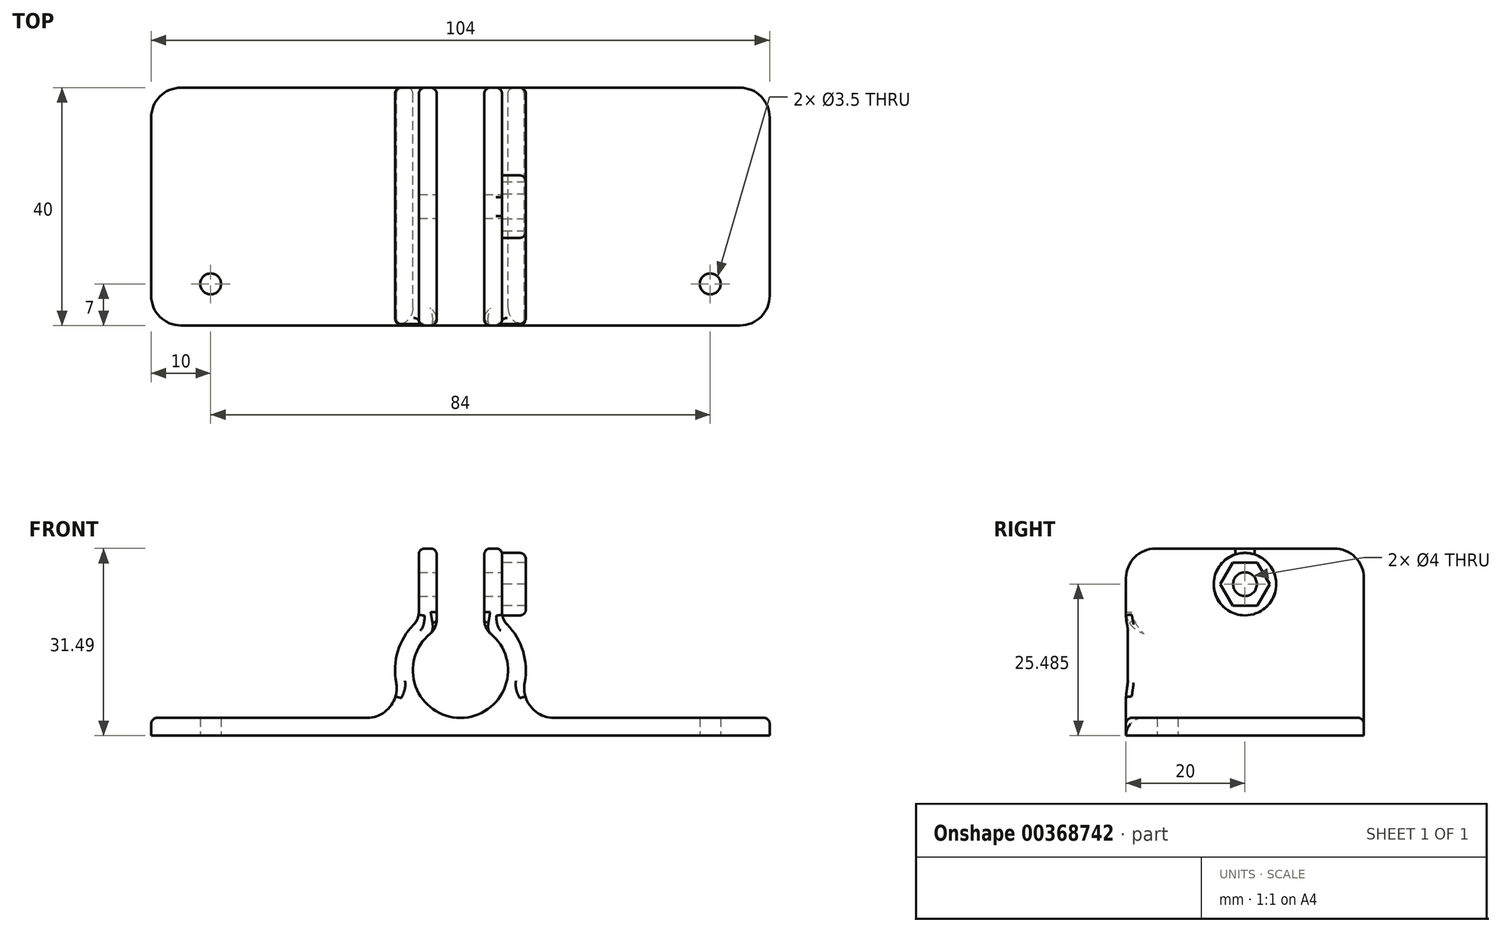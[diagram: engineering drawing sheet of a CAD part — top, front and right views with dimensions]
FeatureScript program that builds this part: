
annotation { "Feature Type Name" : "Feature", "Feature Type Description" : "" }
export const myFeature = defineFeature(function(context is Context, id is Id, definition is map)
    precondition{}
    {
        {
            var Q0;
            Q0=qCreatedBy(makeId("Top.planeOp"),FACE);
            var sketch = newSketch(context, id + "F0", { "sketchPlane" : qUnion([Q0])});
            skLineSegment(sketch, "E0.bottom", {"start": v(-52, 20) * mm, "end": v(52, 20) * mm});
            skLineSegment(sketch, "E0.top", {"start": v(-52, -20) * mm, "end": v(52, -20) * mm});
            skLineSegment(sketch, "E0.left", {"start": v(-52, 20) * mm, "end": v(-52, -20) * mm});
            skLineSegment(sketch, "E0.right", {"start": v(52, 20) * mm, "end": v(52, -20) * mm});
            skPoint(sketch, "E0.middle", {"position": v(0, 0) * mm});
            skLineSegment(sketch, "E1", {"start": v(-63.76, -13) * mm, "end": v(70.54, -13) * mm, "construction": true});
            skCircle(sketch, "E2", {"center": v(-42, -13) * mm, "radius": 1.75 * mm});
            skCircle(sketch, "E3.MirrorC", {"center": v(42, -13) * mm, "radius": 1.75 * mm});
            skSolve(sketch);
        }
        {
            var Q0;
            Q0=qCreatedBy(makeId("Front.planeOp"),FACE);
            cPlane(context, id + "F1", {"entities" : qUnion([Q0]), "cplaneType" : CPlaneType.OFFSET, "offset" : 20 * mm, "oppositeDirection" : true, "width" : 150 * mm, "height" : 150 * mm});
        }
        {
            var Q0;
            Q0=qCreatedBy(id+"F1.planeOp",FACE);
            var sketch = newSketch(context, id + "F2", { "sketchPlane" : qUnion([Q0])});
            skCircle(sketch, "E4", {"center": v(0, 11) * mm, "radius": 11 * mm});
            skPoint(sketch, "E4.first.point", {"position": v(0, 0) * mm});
            skPoint(sketch, "E4.second.point", {"position": v(0, 22) * mm});
            skCircle(sketch, "E5", {"center": v(0, 11) * mm, "radius": 8 * mm});
            skLineSegment(sketch, "E6.bottom", {"start": v(-7, 14.87) * mm, "end": v(-4, 14.87) * mm});
            skLineSegment(sketch, "E6.top", {"start": v(-7, 31.49) * mm, "end": v(-4, 31.49) * mm});
            skLineSegment(sketch, "E6.left", {"start": v(-7, 14.87) * mm, "end": v(-7, 31.49) * mm});
            skLineSegment(sketch, "E6.right", {"start": v(-4, 14.87) * mm, "end": v(-4, 31.49) * mm});
            skPoint(sketch, "E7", {"position": v(-7, 19.49) * mm});
            skLineSegment(sketch, "E8.MirrorCS", {"start": v(4, 14.87) * mm, "end": v(4, 31.49) * mm});
            skLineSegment(sketch, "E9.MirrorCS", {"start": v(7, 31.49) * mm, "end": v(4, 31.49) * mm});
            skLineSegment(sketch, "E10.MirrorCS", {"start": v(7, 14.87) * mm, "end": v(7, 31.49) * mm});
            skLineSegment(sketch, "E11.MirrorCS", {"start": v(7, 14.87) * mm, "end": v(4, 14.87) * mm});
            skSolve(sketch);
        }
        {
            var Q0;
            {var subQ0=sQuery(id+"F2.wireOp",EDGE,"E10.MirrorCS");var subQ1=sQuery(id+"F2.wireOp",EDGE,"E4");var subQ2=makeQuery(id+"F2.imprint","INTERSECT",VERTEX,{"derivedFrom":[subQ1,subQ0]});Q0=makeQuery(id+"F2.imprint","IMPRINT",FACE,{"disambiguationData":[TD([[makeQuery(id+"F2.imprint","IMPRINT",EDGE,{"disambiguationData":[TD([[subQ2,1.0]])],"derivedFrom":subQ1}),1.0]])]});}
            var Q1;
            {var subQ0=sQuery(id+"F2.wireOp",EDGE,"E8.MirrorCS");var subQ1=sQuery(id+"F2.wireOp",EDGE,"E4");var subQ2=makeQuery(id+"F2.imprint","INTERSECT",VERTEX,{"derivedFrom":[subQ1,subQ0]});Q1=makeQuery(id+"F2.imprint","IMPRINT",FACE,{"disambiguationData":[TD([[makeQuery(id+"F2.imprint","IMPRINT",EDGE,{"disambiguationData":[TD([[subQ2,1.0]])],"derivedFrom":subQ1}),1.0]])]});}
            var Q2;
            {var subQ0=sQuery(id+"F2.wireOp",EDGE,"E6.right");var subQ1=sQuery(id+"F2.wireOp",EDGE,"E4");var subQ2=makeQuery(id+"F2.imprint","INTERSECT",VERTEX,{"derivedFrom":[subQ1,subQ0]});Q2=makeQuery(id+"F2.imprint","IMPRINT",FACE,{"disambiguationData":[TD([[makeQuery(id+"F2.imprint","IMPRINT",EDGE,{"disambiguationData":[TD([[subQ2,-1.0]])],"derivedFrom":subQ1}),1.0]])]});}
            var Q3;
            {var subQ0=sQuery(id+"F2.wireOp",EDGE,"E8.MirrorCS");var subQ1=sQuery(id+"F2.wireOp",EDGE,"E4");var subQ2=makeQuery(id+"F2.imprint","INTERSECT",VERTEX,{"derivedFrom":[subQ1,subQ0]});Q3=makeQuery(id+"F2.imprint","IMPRINT",FACE,{"disambiguationData":[TD([[makeQuery(id+"F2.imprint","IMPRINT",EDGE,{"disambiguationData":[TD([[subQ2,1.0]])],"derivedFrom":subQ1}),1.0]])]});}
            var Q4;
            {var subQ0=sQuery(id+"F2.wireOp",EDGE,"E10.MirrorCS");var subQ1=sQuery(id+"F2.wireOp",EDGE,"E4");var subQ2=makeQuery(id+"F2.imprint","INTERSECT",VERTEX,{"derivedFrom":[subQ1,subQ0]});Q4=makeQuery(id+"F2.imprint","IMPRINT",FACE,{"disambiguationData":[TD([[makeQuery(id+"F2.imprint","IMPRINT",EDGE,{"disambiguationData":[TD([[subQ2,1.0]])],"derivedFrom":subQ1}),1.0]])]});}
            var Q5;
            {var subQ0=sQuery(id+"F2.wireOp",EDGE,"E8.MirrorCS");var subQ1=sQuery(id+"F2.wireOp",EDGE,"E4");var subQ2=makeQuery(id+"F2.imprint","INTERSECT",VERTEX,{"derivedFrom":[subQ1,subQ0]});Q5=makeQuery(id+"F2.imprint","IMPRINT",FACE,{"disambiguationData":[TD([[makeQuery(id+"F2.imprint","IMPRINT",EDGE,{"disambiguationData":[TD([[subQ2,1.0]])],"derivedFrom":subQ1}),1.0]])]});}
            var Q6;
            {var subQ0=sQuery(id+"F2.wireOp",EDGE,"E6.right");var subQ1=sQuery(id+"F2.wireOp",EDGE,"E4");var subQ2=makeQuery(id+"F2.imprint","INTERSECT",VERTEX,{"derivedFrom":[subQ1,subQ0]});Q6=makeQuery(id+"F2.imprint","IMPRINT",FACE,{"disambiguationData":[TD([[makeQuery(id+"F2.imprint","IMPRINT",EDGE,{"disambiguationData":[TD([[subQ2,-1.0]])],"derivedFrom":subQ1}),1.0]])]});}
            var Q7;
            {var subQ5=sQuery(id+"F2.wireOp",EDGE,"E6.top");Q7=makeQuery(id+"F2.imprint","IMPRINT",FACE,{"disambiguationData":[TD([[makeQuery(id+"F2.imprint","IMPRINT",EDGE,{"derivedFrom":subQ5}),-1.0]])]});}
            var Q8;
            {var subQ5=sQuery(id+"F2.wireOp",EDGE,"E9.MirrorCS");Q8=makeQuery(id+"F2.imprint","IMPRINT",FACE,{"disambiguationData":[TD([[makeQuery(id+"F2.imprint","IMPRINT",EDGE,{"derivedFrom":subQ5}),1.0]])]});}
            extrude(context, id + "F3", {"entities" : qUnion([Q0, Q1, Q2, Q3, Q4, Q5, Q6, Q7, Q8]), "depth" : 40 * mm});
        }
        {
            var Q0;
            Q0=makeQuery(id+"F0.imprint","IMPRINT",FACE,{"disambiguationData":[TD([[makeQuery(id+"F0.imprint","IMPRINT",EDGE,{"derivedFrom":sQuery(id+"F0.wireOp",EDGE,"E0.bottom")}),-1.0]])]});
            extrude(context, id + "F4", {"entities" : qUnion([Q0]), "operationType" : NewBodyOperationType.ADD, "depth" : 3 * mm});
        }
        {
            var Q0;
            Q0=makeQuery(id+"F4.boolean.opBoolean","INTERSECT",EDGE,{"disambiguationData":[OD(1.0)],"derivedFrom":[makeQuery(id+"F3.opExtrude","SWEPT_FACE",FACE,{"disambiguationData":[OSD([sQuery(id+"F2.wireOp",EDGE,"E4")])]}),makeQuery(id+"F4.opExtrude","CAP_FACE",FACE,{"disambiguationData":[OSD([sQuery(id+"F0.wireOp",EDGE,"E0.bottom"),sQuery(id+"F0.wireOp",EDGE,"E0.top"),sQuery(id+"F0.wireOp",EDGE,"E0.left"),sQuery(id+"F0.wireOp",EDGE,"E0.right"),sQuery(id+"F0.wireOp",EDGE,"E2"),sQuery(id+"F0.wireOp",EDGE,"E3.MirrorC")])],"isStart":false})]});
            var Q1;
            Q1=makeQuery(id+"F4.boolean.opBoolean","INTERSECT",EDGE,{"disambiguationData":[OD(0.0)],"derivedFrom":[makeQuery(id+"F3.opExtrude","SWEPT_FACE",FACE,{"disambiguationData":[OSD([sQuery(id+"F2.wireOp",EDGE,"E4")])]}),makeQuery(id+"F4.opExtrude","CAP_FACE",FACE,{"disambiguationData":[OSD([sQuery(id+"F0.wireOp",EDGE,"E0.bottom"),sQuery(id+"F0.wireOp",EDGE,"E0.top"),sQuery(id+"F0.wireOp",EDGE,"E0.left"),sQuery(id+"F0.wireOp",EDGE,"E0.right"),sQuery(id+"F0.wireOp",EDGE,"E2"),sQuery(id+"F0.wireOp",EDGE,"E3.MirrorC")])],"isStart":false})]});
            var Q2;
            Q2=makeQuery(id+"F4.opExtrude","SWEPT_EDGE",EDGE,{"disambiguationData":[OSD([sQuery(id+"F0.wireOp",EDGE,"E0.bottom"),sQuery(id+"F0.wireOp",EDGE,"E0.left")])]});
            var Q3;
            Q3=makeQuery(id+"F4.opExtrude","SWEPT_EDGE",EDGE,{"disambiguationData":[OSD([sQuery(id+"F0.wireOp",EDGE,"E0.bottom"),sQuery(id+"F0.wireOp",EDGE,"E0.right")])]});
            var Q4;
            Q4=makeQuery(id+"F4.opExtrude","SWEPT_EDGE",EDGE,{"disambiguationData":[OSD([sQuery(id+"F0.wireOp",EDGE,"E0.top"),sQuery(id+"F0.wireOp",EDGE,"E0.right")])]});
            var Q5;
            Q5=makeQuery(id+"F4.opExtrude","SWEPT_EDGE",EDGE,{"disambiguationData":[OSD([sQuery(id+"F0.wireOp",EDGE,"E0.top"),sQuery(id+"F0.wireOp",EDGE,"E0.left")])]});
            var Q6;
            Q6=makeQuery(id+"F3.opExtrude","CAP_EDGE",EDGE,{"disambiguationData":[OSD([sQuery(id+"F2.wireOp",EDGE,"E9.MirrorCS")])],"isStart":false});
            var Q7;
            Q7=makeQuery(id+"F3.opExtrude","CAP_EDGE",EDGE,{"disambiguationData":[OSD([sQuery(id+"F2.wireOp",EDGE,"E6.top")])],"isStart":false});
            var Q8;
            Q8=makeQuery(id+"F3.opExtrude","CAP_EDGE",EDGE,{"disambiguationData":[OSD([sQuery(id+"F2.wireOp",EDGE,"E9.MirrorCS")])],"isStart":true});
            var Q9;
            Q9=makeQuery(id+"F3.opExtrude","CAP_EDGE",EDGE,{"disambiguationData":[OSD([sQuery(id+"F2.wireOp",EDGE,"E6.top")])],"isStart":true});
            fillet(context, id + "F5", {"entities" : qUnion([Q0, Q1, Q2, Q3, Q4, Q5, Q6, Q7, Q8, Q9]), "radius" : 5 * mm, "tangentPropagation" : true, "allowEdgeOverflow" : false});
        }
        {
            var Q0;
            Q0=makeQuery(id+"F3.opExtrude","SWEPT_FACE",FACE,{"disambiguationData":[OSD([sQuery(id+"F2.wireOp",EDGE,"E10.MirrorCS")])]});
            var sketch = newSketch(context, id + "F6", { "sketchPlane" : qUnion([Q0])});
            skCircle(sketch, "E12", {"center": v(0, 25.49) * mm, "radius": 2 * mm});
            skCircle(sketch, "E13.cCircle", {"center": v(0, 25.49) * mm, "radius": 3.6 * mm, "construction": true});
            skLineSegment(sketch, "E13.0", {"start": v(2.08, 29.09) * mm, "end": v(4.16, 25.49) * mm});
            skLineSegment(sketch, "E13.1", {"start": v(4.16, 25.49) * mm, "end": v(2.08, 21.89) * mm});
            skLineSegment(sketch, "E13.2", {"start": v(2.08, 21.89) * mm, "end": v(-2.08, 21.89) * mm});
            skLineSegment(sketch, "E13.3", {"start": v(-2.08, 21.89) * mm, "end": v(-4.16, 25.49) * mm});
            skLineSegment(sketch, "E13.4", {"start": v(-4.16, 25.49) * mm, "end": v(-2.08, 29.09) * mm});
            skLineSegment(sketch, "E13.5", {"start": v(-2.08, 29.09) * mm, "end": v(2.08, 29.09) * mm});
            skPoint(sketch, "E13.0.midPoint", {"position": v(3.12, 27.29) * mm});
            skCircle(sketch, "E14", {"center": v(0, 25.49) * mm, "radius": 5.25 * mm});
            skSolve(sketch);
        }
        {
            var Q0;
            Q0=makeQuery(id+"F6.imprint","IMPRINT",FACE,{"disambiguationData":[TD([[makeQuery(id+"F6.imprint","IMPRINT",EDGE,{"derivedFrom":sQuery(id+"F6.wireOp",EDGE,"E12")}),1.0]])]});
            extrude(context, id + "F7", {"entities" : qUnion([Q0]), "operationType" : NewBodyOperationType.REMOVE, "oppositeDirection" : true, "depth" : 25 * mm});
        }
        {
            var Q0;
            Q0=makeQuery(id+"F6.imprint","IMPRINT",FACE,{"disambiguationData":[TD([[makeQuery(id+"F6.imprint","IMPRINT",EDGE,{"derivedFrom":sQuery(id+"F6.wireOp",EDGE,"E13.0")}),1.0]])]});
            extrude(context, id + "F8", {"entities" : qUnion([Q0]), "operationType" : NewBodyOperationType.ADD, "depth" : 4 * mm});
        }
        {
            var Q0;
            Q0=makeQuery(id+"F3.opExtrude","CAP_EDGE",EDGE,{"disambiguationData":[OSD([sQuery(id+"F2.wireOp",EDGE,"E5")])],"isStart":false});
            var Q1;
            Q1=makeQuery(id+"F3.opExtrude","SWEPT_EDGE",EDGE,{"disambiguationData":[OSD([sQuery(id+"F2.wireOp",EDGE,"E4"),sQuery(id+"F2.wireOp",EDGE,"E10.MirrorCS")])]});
            var Q2;
            Q2=makeQuery(id+"F3.opExtrude","SWEPT_EDGE",EDGE,{"disambiguationData":[OSD([sQuery(id+"F2.wireOp",EDGE,"E4"),sQuery(id+"F2.wireOp",EDGE,"E6.left")])]});
            var Q3;
            Q3=makeQuery(id+"F3.opExtrude","SWEPT_EDGE",EDGE,{"disambiguationData":[OSD([sQuery(id+"F2.wireOp",EDGE,"E5"),sQuery(id+"F2.wireOp",EDGE,"E6.right")])]});
            var Q4;
            Q4=makeQuery(id+"F3.opExtrude","SWEPT_EDGE",EDGE,{"disambiguationData":[OSD([sQuery(id+"F2.wireOp",EDGE,"E5"),sQuery(id+"F2.wireOp",EDGE,"E8.MirrorCS")])]});
            fillet(context, id + "F9", {"entities" : qUnion([Q0, Q1, Q2, Q3, Q4]), "radius" : 3 * mm, "tangentPropagation" : true, "allowEdgeOverflow" : false});
        }
        {
            var Q0;
            {var subQ0=sQuery(id+"F0.wireOp",EDGE,"E0.left");var subQ1=sQuery(id+"F0.wireOp",EDGE,"E0.bottom");Q0=makeQuery(id+"F4.boolean.opBoolean","SPLIT",EDGE,{"disambiguationData":[TD([makeQuery(id+"F4.opExtrude","SWEPT_FACE",FACE,{"disambiguationData":[OSD([subQ0])]})])],"derivedFrom":makeQuery(id+"F4.opExtrude","CAP_EDGE",EDGE,{"disambiguationData":[OSD([subQ1])],"isStart":false})});}
            var Q1;
            {var subQ0=sQuery(id+"F0.wireOp",EDGE,"E0.right");var subQ1=sQuery(id+"F0.wireOp",EDGE,"E0.bottom");Q1=makeQuery(id+"F4.boolean.opBoolean","SPLIT",EDGE,{"disambiguationData":[TD([makeQuery(id+"F4.opExtrude","SWEPT_FACE",FACE,{"disambiguationData":[OSD([subQ0])]})])],"derivedFrom":makeQuery(id+"F4.opExtrude","CAP_EDGE",EDGE,{"disambiguationData":[OSD([subQ1])],"isStart":false})});}
            var Q2;
            Q2=makeQuery(id+"F3.opExtrude","SWEPT_EDGE",EDGE,{"disambiguationData":[OSD([sQuery(id+"F2.wireOp",EDGE,"E8.MirrorCS"),sQuery(id+"F2.wireOp",EDGE,"E9.MirrorCS")])]});
            fillet(context, id + "F10", {"entities" : qUnion([Q0, Q1, Q2]), "radius" : 1 * mm, "tangentPropagation" : true, "allowEdgeOverflow" : false});
        }
        {
            var Q0;
            Q0=makeQuery(id+"F8.opExtrude","CAP_EDGE",EDGE,{"disambiguationData":[OSD([sQuery(id+"F6.wireOp",EDGE,"E14")])],"isStart":false});
            var Q1;
            Q1=makeQuery(id+"F8.opExtrude","CAP_EDGE",EDGE,{"disambiguationData":[OSD([sQuery(id+"F6.wireOp",EDGE,"E14")])],"isStart":true});
            fillet(context, id + "F11", {"entities" : qUnion([Q0, Q1]), "radius" : 1 * mm, "tangentPropagation" : true, "allowEdgeOverflow" : false});
        }
    });
